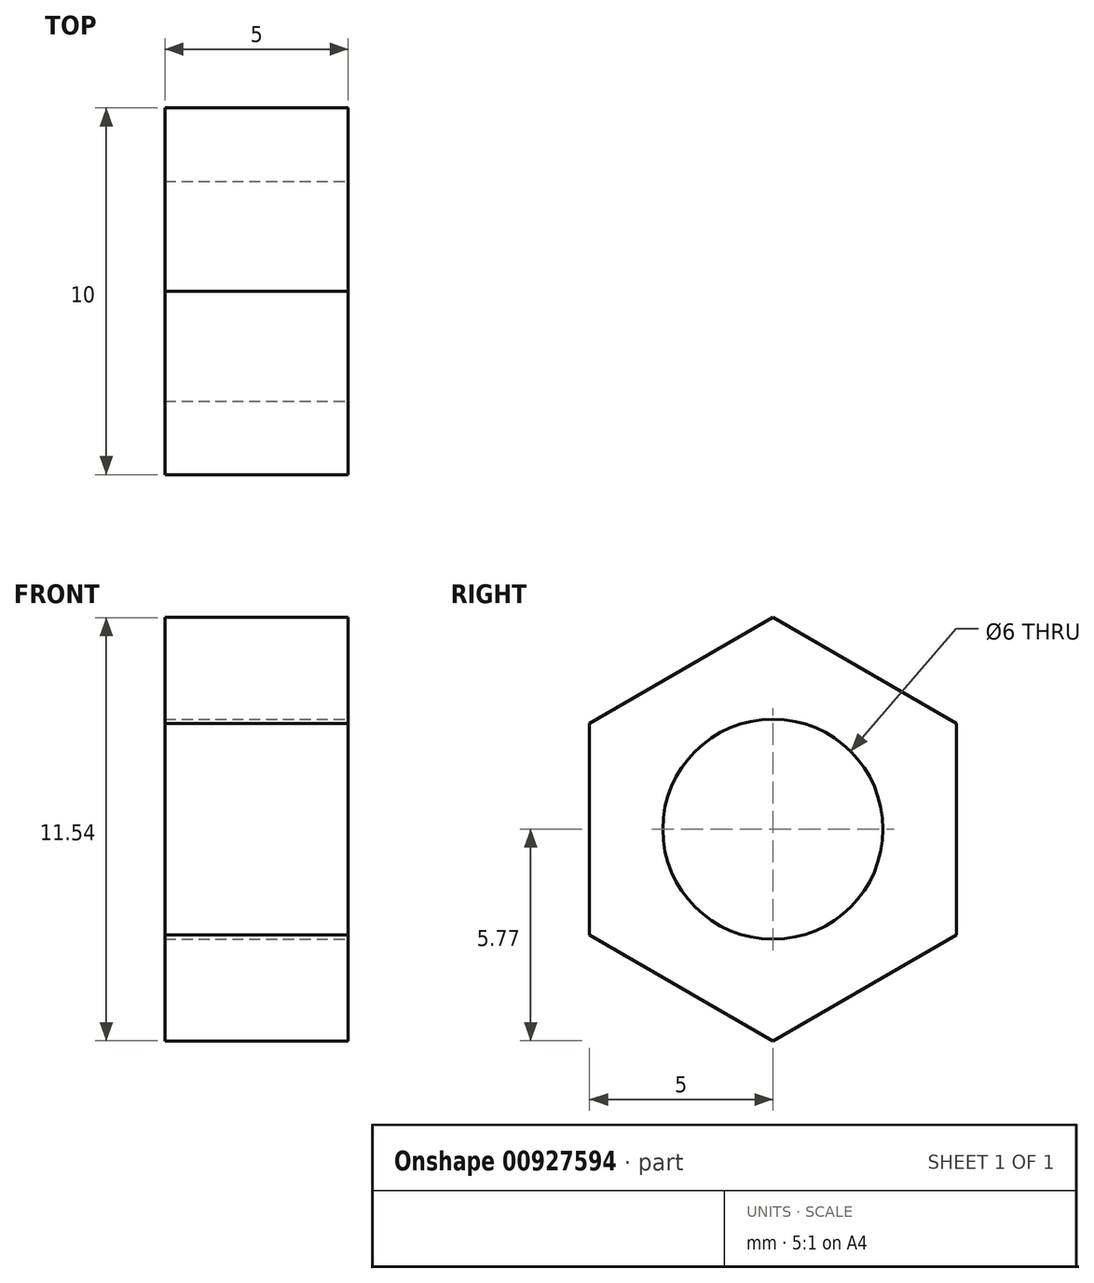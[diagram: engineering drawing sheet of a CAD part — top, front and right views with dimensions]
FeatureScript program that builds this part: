
annotation { "Feature Type Name" : "Feature", "Feature Type Description" : "" }
export const myFeature = defineFeature(function(context is Context, id is Id, definition is map)
    precondition{}
    {
        {
            var Q0;
            Q0=qCreatedBy(makeId("Right.planeOp"),FACE);
            var sketch = newSketch(context, id + "F0", { "sketchPlane" : qUnion([Q0])});
            skCircle(sketch, "E0.cCircle", {"center": v(0, 0) * mm, "radius": 5 * mm, "construction": true});
            skLineSegment(sketch, "E0.0", {"start": v(5, -2.89) * mm, "end": v(0, -5.77) * mm});
            skLineSegment(sketch, "E0.1", {"start": v(0, -5.77) * mm, "end": v(-5, -2.89) * mm});
            skLineSegment(sketch, "E0.2", {"start": v(-5, -2.89) * mm, "end": v(-5, 2.89) * mm});
            skLineSegment(sketch, "E0.3", {"start": v(-5, 2.89) * mm, "end": v(0, 5.77) * mm});
            skLineSegment(sketch, "E0.4", {"start": v(0, 5.77) * mm, "end": v(5, 2.89) * mm});
            skLineSegment(sketch, "E0.5", {"start": v(5, 2.89) * mm, "end": v(5, -2.89) * mm});
            skPoint(sketch, "E0.0.midPoint", {"position": v(2.5, -4.33) * mm});
            skLineSegment(sketch, "E1", {"start": v(0, -15.13) * mm, "end": v(0, 13.62) * mm, "construction": true});
            skSolve(sketch);
        }
        {
            var Q0;
            Q0 = qSketchRegion(id + "F0", true);
            extrude(context, id + "F1", {"entities" : qUnion([Q0]), "depth" : 5 * mm, "offsetDistance" : 25 * mm});
        }
        {
            var Q0;
            Q0=makeQuery(id+"F1.opExtrude","CAP_FACE",FACE,{"disambiguationData":[OSD([sQuery(id+"F0.wireOp",EDGE,"E0.0"),sQuery(id+"F0.wireOp",EDGE,"E0.1"),sQuery(id+"F0.wireOp",EDGE,"E0.2"),sQuery(id+"F0.wireOp",EDGE,"E0.3"),sQuery(id+"F0.wireOp",EDGE,"E0.4"),sQuery(id+"F0.wireOp",EDGE,"E0.5")])],"isStart":false});
            var sketch = newSketch(context, id + "F2", { "sketchPlane" : qUnion([Q0])});
            skCircle(sketch, "E2", {"center": v(0, 0) * mm, "radius": 3 * mm});
            skSolve(sketch);
        }
        {
            var Q0;
            Q0 = qSketchRegion(id + "F2", true);
            extrude(context, id + "F3", {"entities" : qUnion([Q0]), "operationType" : NewBodyOperationType.REMOVE, "oppositeDirection" : true, "depth" : 25 * mm, "offsetDistance" : 25 * mm});
        }
    });
